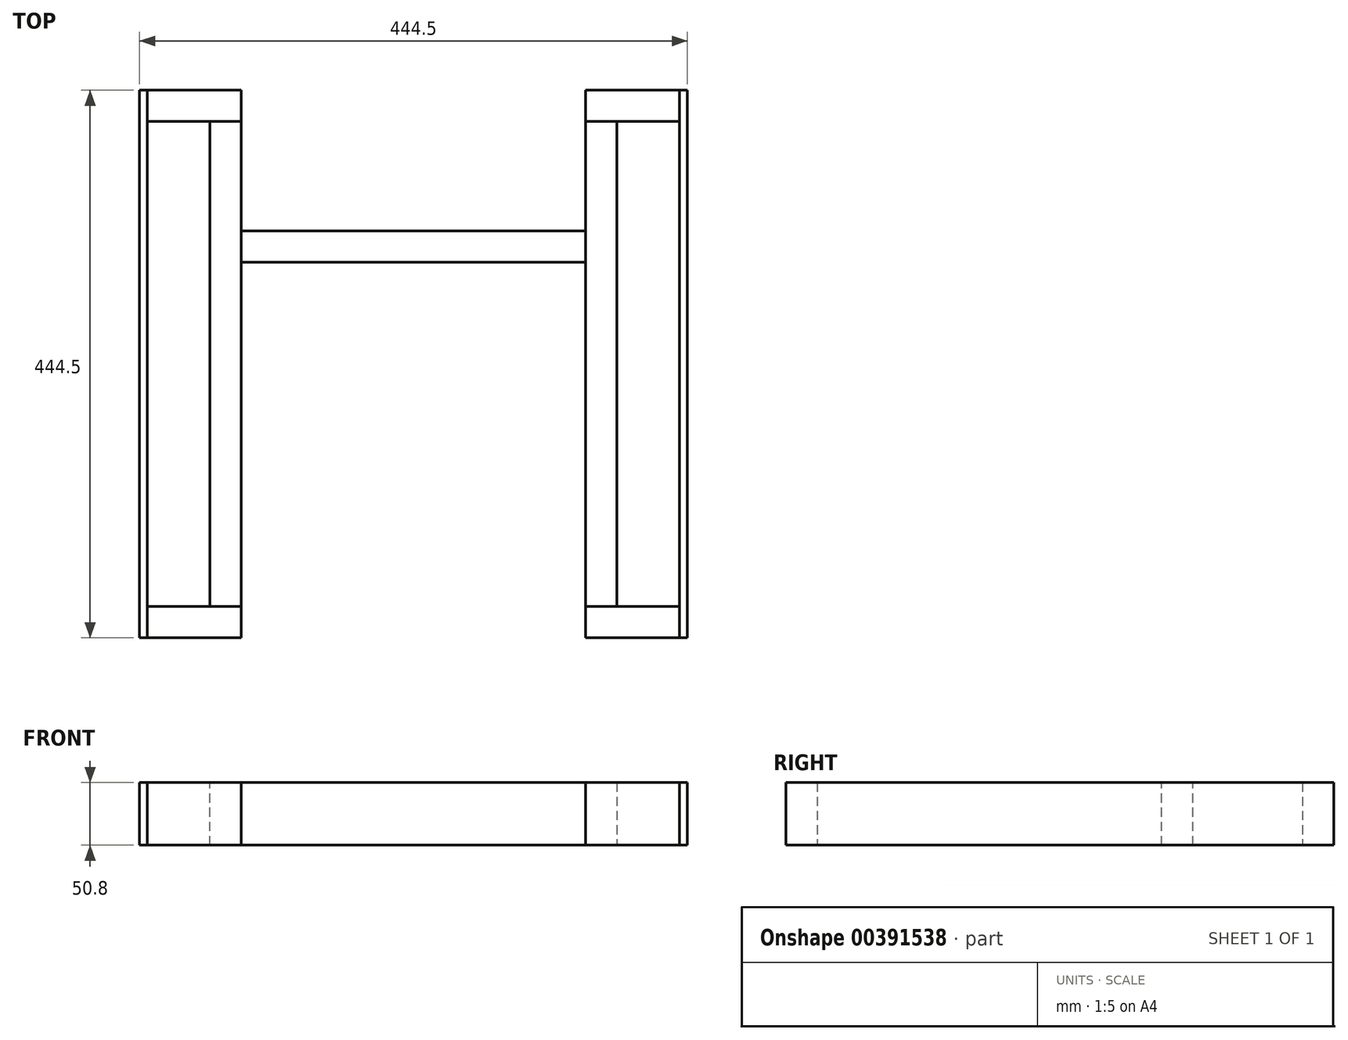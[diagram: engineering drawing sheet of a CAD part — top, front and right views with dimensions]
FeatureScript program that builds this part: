
annotation { "Feature Type Name" : "Feature", "Feature Type Description" : "" }
export const myFeature = defineFeature(function(context is Context, id is Id, definition is map)
    precondition{}
    {
        {
            var Q0;
            Q0=qCreatedBy(makeId("Top.planeOp"),FACE);
            var sketch = newSketch(context, id + "F0", { "sketchPlane" : qUnion([Q0])});
            skLineSegment(sketch, "E0.bottom", {"start": v(222.25, -222.25) * mm, "end": v(-222.25, -222.25) * mm, "construction": true});
            skLineSegment(sketch, "E0.top", {"start": v(222.25, 222.25) * mm, "end": v(-222.25, 222.25) * mm, "construction": true});
            skLineSegment(sketch, "E0.left", {"start": v(222.25, -222.25) * mm, "end": v(222.25, 222.25) * mm, "construction": true});
            skLineSegment(sketch, "E0.right", {"start": v(-222.25, -222.25) * mm, "end": v(-222.25, 222.25) * mm, "construction": true});
            skPoint(sketch, "E0.middle", {"position": v(0, 0) * mm});
            skLineSegment(sketch, "E1.bottom", {"start": v(-139.7, 222.25) * mm, "end": v(-215.9, 222.25) * mm});
            skLineSegment(sketch, "E1.top", {"start": v(-139.7, 196.85) * mm, "end": v(-215.9, 196.85) * mm});
            skLineSegment(sketch, "E1.left", {"start": v(-139.7, 222.25) * mm, "end": v(-139.7, 196.85) * mm});
            skLineSegment(sketch, "E1.right", {"start": v(-215.9, 222.25) * mm, "end": v(-215.9, 196.85) * mm});
            skLineSegment(sketch, "E2.MirrorCS", {"start": v(139.7, 196.85) * mm, "end": v(215.9, 196.85) * mm});
            skLineSegment(sketch, "E3.MirrorCS", {"start": v(139.7, 222.25) * mm, "end": v(139.7, 196.85) * mm});
            skLineSegment(sketch, "E4.MirrorCS", {"start": v(139.7, 222.25) * mm, "end": v(215.9, 222.25) * mm});
            skLineSegment(sketch, "E5.MirrorCS", {"start": v(215.9, 222.25) * mm, "end": v(215.9, 196.85) * mm});
            skLineSegment(sketch, "E6.MirrorCS", {"start": v(-139.7, -196.85) * mm, "end": v(-215.9, -196.85) * mm});
            skLineSegment(sketch, "E7.MirrorCS", {"start": v(-139.7, -222.25) * mm, "end": v(-139.7, -196.85) * mm});
            skLineSegment(sketch, "E8.MirrorCS", {"start": v(-139.7, -222.25) * mm, "end": v(-215.9, -222.25) * mm});
            skLineSegment(sketch, "E9.MirrorCS", {"start": v(-215.9, -222.25) * mm, "end": v(-215.9, -196.85) * mm});
            skLineSegment(sketch, "E10.MirrorCS", {"start": v(139.7, -196.85) * mm, "end": v(215.9, -196.85) * mm});
            skLineSegment(sketch, "E11.MirrorCS", {"start": v(215.9, -222.25) * mm, "end": v(215.9, -196.85) * mm});
            skLineSegment(sketch, "E12.MirrorCS", {"start": v(139.7, -222.25) * mm, "end": v(215.9, -222.25) * mm});
            skLineSegment(sketch, "E13.MirrorCS", {"start": v(139.7, -222.25) * mm, "end": v(139.7, -196.85) * mm});
            skSolve(sketch);
        }
        {
            var Q0;
            Q0=qCreatedBy(makeId("Front.planeOp"),FACE);
            var sketch = newSketch(context, id + "F1", { "sketchPlane" : qUnion([Q0])});
            skLineSegment(sketch, "E14.bottom", {"start": v(-222.25, 88.9) * mm, "end": v(-215.9, 88.9) * mm});
            skLineSegment(sketch, "E14.top", {"start": v(-222.25, 38.1) * mm, "end": v(-215.9, 38.1) * mm});
            skLineSegment(sketch, "E14.left", {"start": v(-222.25, 88.9) * mm, "end": v(-222.25, 38.1) * mm});
            skLineSegment(sketch, "E14.right", {"start": v(-215.9, 88.9) * mm, "end": v(-215.9, 38.1) * mm});
            skLineSegment(sketch, "E15.MirrorCS", {"start": v(215.9, 88.9) * mm, "end": v(215.9, 38.1) * mm});
            skLineSegment(sketch, "E16.MirrorCS", {"start": v(222.25, 88.9) * mm, "end": v(215.9, 88.9) * mm});
            skLineSegment(sketch, "E17.MirrorCS", {"start": v(222.25, 88.9) * mm, "end": v(222.25, 38.1) * mm});
            skLineSegment(sketch, "E18.MirrorCS", {"start": v(222.25, 38.1) * mm, "end": v(215.9, 38.1) * mm});
            skLineSegment(sketch, "E19.bottom", {"start": v(-165.1, 38.1) * mm, "end": v(-139.7, 38.1) * mm});
            skLineSegment(sketch, "E19.top", {"start": v(-165.1, 88.9) * mm, "end": v(-139.7, 88.9) * mm});
            skLineSegment(sketch, "E19.left", {"start": v(-165.1, 38.1) * mm, "end": v(-165.1, 88.9) * mm});
            skLineSegment(sketch, "E19.right", {"start": v(-139.7, 38.1) * mm, "end": v(-139.7, 88.9) * mm});
            skLineSegment(sketch, "E20.MirrorCS", {"start": v(139.7, 38.1) * mm, "end": v(139.7, 88.9) * mm});
            skLineSegment(sketch, "E21.MirrorCS", {"start": v(165.1, 88.9) * mm, "end": v(139.7, 88.9) * mm});
            skLineSegment(sketch, "E22.MirrorCS", {"start": v(165.1, 38.1) * mm, "end": v(165.1, 88.9) * mm});
            skLineSegment(sketch, "E23.MirrorCS", {"start": v(165.1, 38.1) * mm, "end": v(139.7, 38.1) * mm});
            skSolve(sketch);
        }
        {
            var Q0;
            Q0 = qSketchRegion(id + "F1", true);
            extrude(context, id + "F2", {"entities" : qUnion([Q0]), "endBound" : BoundingType.SYMMETRIC, "depth" : 444.5 * mm});
        }
        {
            var Q0;
            Q0=makeQuery(id+"F0.imprint","IMPRINT",FACE,{"disambiguationData":[TD([[makeQuery(id+"F0.imprint","IMPRINT",EDGE,{"derivedFrom":sQuery(id+"F0.wireOp",EDGE,"E1.bottom")}),1.0]])]});
            var Q1;
            Q1=makeQuery(id+"F0.imprint","IMPRINT",FACE,{"disambiguationData":[TD([[makeQuery(id+"F0.imprint","IMPRINT",EDGE,{"derivedFrom":sQuery(id+"F0.wireOp",EDGE,"E2.MirrorCS")}),1.0]])]});
            var Q2;
            Q2=makeQuery(id+"F0.imprint","IMPRINT",FACE,{"disambiguationData":[TD([[makeQuery(id+"F0.imprint","IMPRINT",EDGE,{"derivedFrom":sQuery(id+"F0.wireOp",EDGE,"E10.MirrorCS")}),-1.0]])]});
            var Q3;
            Q3=makeQuery(id+"F0.imprint","IMPRINT",FACE,{"disambiguationData":[TD([[makeQuery(id+"F0.imprint","IMPRINT",EDGE,{"derivedFrom":sQuery(id+"F0.wireOp",EDGE,"E6.MirrorCS")}),1.0]])]});
            extrude(context, id + "F3", {"entities" : qUnion([Q0, Q1, Q2, Q3]), "operationType" : NewBodyOperationType.REMOVE, "depth" : 176.53 * mm});
        }
        {
            var Q0;
            Q0=makeQuery(id+"F2.opExtrude","SWEPT_FACE",FACE,{"disambiguationData":[OSD([sQuery(id+"F1.wireOp",EDGE,"E19.top")])]});
            var sketch = newSketch(context, id + "F4", { "sketchPlane" : qUnion([Q0])});
            skPoint(sketch, "E24.0", {"position": v(-215.9, 222.25) * mm});
            skPoint(sketch, "E25.0", {"position": v(-139.7, 196.85) * mm});
            skLineSegment(sketch, "E26.bottom", {"start": v(-215.9, 222.25) * mm, "end": v(-139.7, 222.25) * mm});
            skLineSegment(sketch, "E26.top", {"start": v(-215.9, 196.85) * mm, "end": v(-139.7, 196.85) * mm});
            skLineSegment(sketch, "E26.left", {"start": v(-215.9, 222.25) * mm, "end": v(-215.9, 196.85) * mm});
            skLineSegment(sketch, "E26.right", {"start": v(-139.7, 222.25) * mm, "end": v(-139.7, 196.85) * mm});
            skLineSegment(sketch, "E27.MirrorCS", {"start": v(139.7, 222.25) * mm, "end": v(139.7, 196.85) * mm});
            skLineSegment(sketch, "E28.MirrorCS", {"start": v(215.9, 222.25) * mm, "end": v(139.7, 222.25) * mm});
            skLineSegment(sketch, "E29.MirrorCS", {"start": v(215.9, 196.85) * mm, "end": v(139.7, 196.85) * mm});
            skLineSegment(sketch, "E30.MirrorCS", {"start": v(215.9, 222.25) * mm, "end": v(215.9, 196.85) * mm});
            skLineSegment(sketch, "E31.MirrorCS", {"start": v(-215.9, -196.85) * mm, "end": v(-139.7, -196.85) * mm});
            skLineSegment(sketch, "E32.MirrorCS", {"start": v(-215.9, -222.25) * mm, "end": v(-139.7, -222.25) * mm});
            skLineSegment(sketch, "E33.MirrorCS", {"start": v(-215.9, -222.25) * mm, "end": v(-215.9, -196.85) * mm});
            skLineSegment(sketch, "E34.MirrorCS", {"start": v(-139.7, -222.25) * mm, "end": v(-139.7, -196.85) * mm});
            skLineSegment(sketch, "E35.MirrorCS", {"start": v(139.7, -222.25) * mm, "end": v(139.7, -196.85) * mm});
            skLineSegment(sketch, "E36.MirrorCS", {"start": v(215.9, -222.25) * mm, "end": v(139.7, -222.25) * mm});
            skLineSegment(sketch, "E37.MirrorCS", {"start": v(215.9, -196.85) * mm, "end": v(139.7, -196.85) * mm});
            skLineSegment(sketch, "E38.MirrorCS", {"start": v(215.9, -222.25) * mm, "end": v(215.9, -196.85) * mm});
            skLineSegment(sketch, "E39.bottom", {"start": v(-139.7, 82.55) * mm, "end": v(139.7, 82.55) * mm});
            skLineSegment(sketch, "E39.top", {"start": v(-139.7, 107.95) * mm, "end": v(139.7, 107.95) * mm});
            skLineSegment(sketch, "E39.left", {"start": v(-139.7, 82.55) * mm, "end": v(-139.7, 107.95) * mm});
            skLineSegment(sketch, "E39.right", {"start": v(139.7, 82.55) * mm, "end": v(139.7, 107.95) * mm});
            skSolve(sketch);
        }
        {
            var Q0;
            Q0=makeQuery(id+"F4.imprint","IMPRINT",FACE,{"disambiguationData":[TD([[makeQuery(id+"F4.imprint","IMPRINT",EDGE,{"derivedFrom":sQuery(id+"F4.wireOp",EDGE,"E26.bottom")}),-1.0]])]});
            var Q1;
            Q1=makeQuery(id+"F4.imprint","IMPRINT",FACE,{"disambiguationData":[TD([[makeQuery(id+"F4.imprint","IMPRINT",EDGE,{"derivedFrom":sQuery(id+"F4.wireOp",EDGE,"E32.MirrorCS")}),1.0]])]});
            var Q2;
            Q2=makeQuery(id+"F4.imprint","IMPRINT",FACE,{"disambiguationData":[TD([[makeQuery(id+"F4.imprint","IMPRINT",EDGE,{"derivedFrom":sQuery(id+"F4.wireOp",EDGE,"E35.MirrorCS")}),-1.0]])]});
            var Q3;
            Q3=makeQuery(id+"F4.imprint","IMPRINT",FACE,{"disambiguationData":[TD([[makeQuery(id+"F4.imprint","IMPRINT",EDGE,{"derivedFrom":sQuery(id+"F4.wireOp",EDGE,"E27.MirrorCS")}),1.0]])]});
            var Q4;
            Q4=makeQuery(id+"F4.imprint","IMPRINT",FACE,{"disambiguationData":[TD([[makeQuery(id+"F4.imprint","IMPRINT",EDGE,{"derivedFrom":sQuery(id+"F4.wireOp",EDGE,"E39.bottom")}),1.0]])]});
            extrude(context, id + "F5", {"entities" : qUnion([Q0, Q1, Q2, Q3, Q4]), "oppositeDirection" : true, "depth" : 50.8 * mm});
        }
    });
